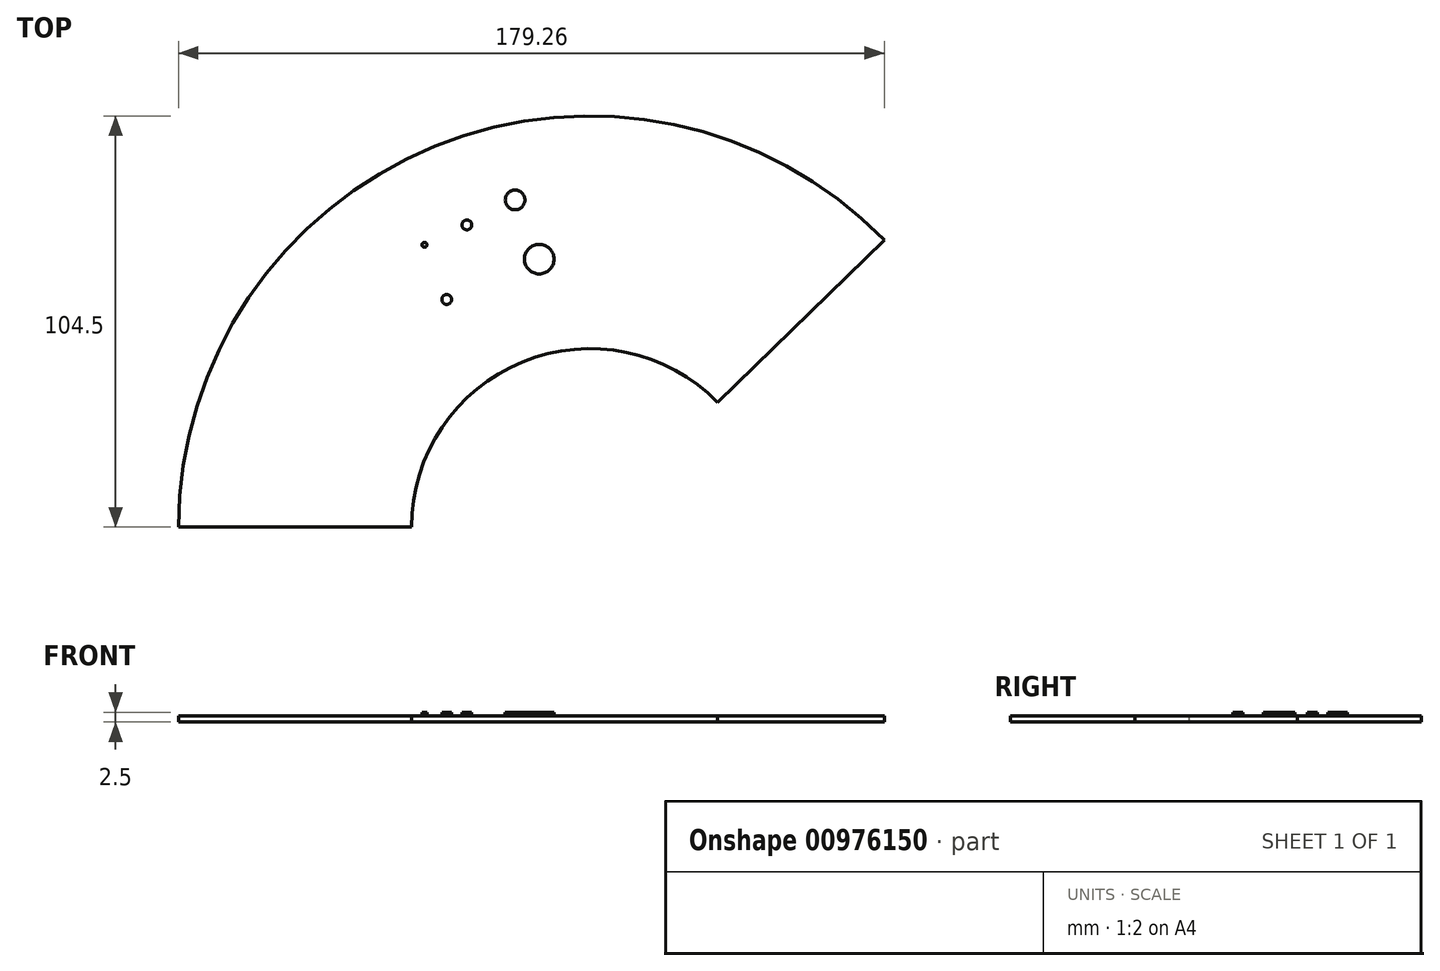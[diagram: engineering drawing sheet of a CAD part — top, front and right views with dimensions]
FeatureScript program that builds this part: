
annotation { "Feature Type Name" : "Feature", "Feature Type Description" : "" }
export const myFeature = defineFeature(function(context is Context, id is Id, definition is map)
    precondition{}
    {
        {
            var Q0;
            Q0=qCreatedBy(makeId("Top.planeOp"),FACE);
            var sketch = newSketch(context, id + "F0", { "sketchPlane" : qUnion([Q0])});
            skArc(sketch, "E0", {"start": v(74.76, 73.01) * mm, "mid": v(-39.42, 96.78) * mm, "end": v(-104.5, 0) * mm});
            skArc(sketch, "E1", {"start": v(32.44, 31.69) * mm, "mid": v(-17.1, 42) * mm, "end": v(-45.35, 0) * mm});
            skLineSegment(sketch, "E2", {"start": v(-45.35, 0) * mm, "end": v(-104.5, 0) * mm});
            skLineSegment(sketch, "E3", {"start": v(32.44, 31.69) * mm, "end": v(74.76, 73.01) * mm});
            skSolve(sketch);
        }
        {
            var Q0;
            Q0=qSketchRegion(id+"F0",true);
            extrude(context, id + "F1", {"entities" : qUnion([Q0]), "depth" : 1.5 * mm, "offsetDistance" : 25 * mm});
        }
        {
            var Q0;
            Q0=makeQuery(id+"F1.opExtrude","CAP_FACE",FACE,{"disambiguationData":[OSD([sQuery(id+"F0.wireOp",EDGE,"E0"),sQuery(id+"F0.wireOp",EDGE,"E1"),sQuery(id+"F0.wireOp",EDGE,"E2"),sQuery(id+"F0.wireOp",EDGE,"E3")])],"isStart":false});
            var sketch = newSketch(context, id + "F2", { "sketchPlane" : qUnion([Q0])});
            skLineSegment(sketch, "E4", {"start": v(-17.1, 42) * mm, "end": v(-39.42, 96.78) * mm});
            skPoint(sketch, "E5.center", {"position": v(0, 0) * mm});
            skLineSegment(sketch, "E6", {"start": v(-30.81, 75.65) * mm, "end": v(-29.65, 76.12) * mm});
            skLineSegment(sketch, "E7", {"start": v(-31.97, 75.18) * mm, "end": v(-30.81, 75.65) * mm});
            skLineSegment(sketch, "E8", {"start": v(-30.81, 75.65) * mm, "end": v(-5.95, 85.78) * mm, "construction": true});
            skLineSegment(sketch, "E9", {"start": v(-21.3, 82.13) * mm, "end": v(-21.37, 82.29) * mm});
            skLineSegment(sketch, "E10", {"start": v(-15.76, 81.78) * mm, "end": v(-20.4, 79.9) * mm});
            skLineSegment(sketch, "E11", {"start": v(-30.81, 75.65) * mm, "end": v(-39.42, 72.14) * mm, "construction": true});
            skCircle(sketch, "E12", {"center": v(-42.06, 71.75) * mm, "radius": 0.62 * mm});
            skCircle(sketch, "E13", {"center": v(-31.28, 76.8) * mm, "radius": 1.25 * mm});
            skCircle(sketch, "E14", {"center": v(-19.02, 83.15) * mm, "radius": 2.5 * mm});
            skLineSegment(sketch, "E15", {"start": v(-42.06, 71.75) * mm, "end": v(-41.82, 71.17) * mm, "construction": true});
            skLineSegment(sketch, "E16", {"start": v(-41.82, 71.17) * mm, "end": v(-36.4, 57.85) * mm, "construction": true});
            skLineSegment(sketch, "E17", {"start": v(-19.02, 83.15) * mm, "end": v(-18.08, 80.84) * mm, "construction": true});
            skLineSegment(sketch, "E18", {"start": v(-18.08, 80.84) * mm, "end": v(-12.9, 68.1) * mm, "construction": true});
            skCircle(sketch, "E19", {"center": v(-36.4, 57.85) * mm, "radius": 1.25 * mm});
            skCircle(sketch, "E20", {"center": v(-12.9, 68.1) * mm, "radius": 3.75 * mm});
            skPoint(sketch, "E21.orphan", {"position": v(-42.39, 70.94) * mm});
            skPoint(sketch, "E22.end.orphan", {"position": v(-41.23, 71.4) * mm});
            skSolve(sketch);
        }
        {
            var Q0;
            Q0 = qSketchRegion(id + "F2", true);
            extrude(context, id + "F3", {"entities" : qUnion([Q0]), "operationType" : NewBodyOperationType.ADD, "depth" : 1 * mm, "offsetDistance" : 25 * mm});
        }
    });
